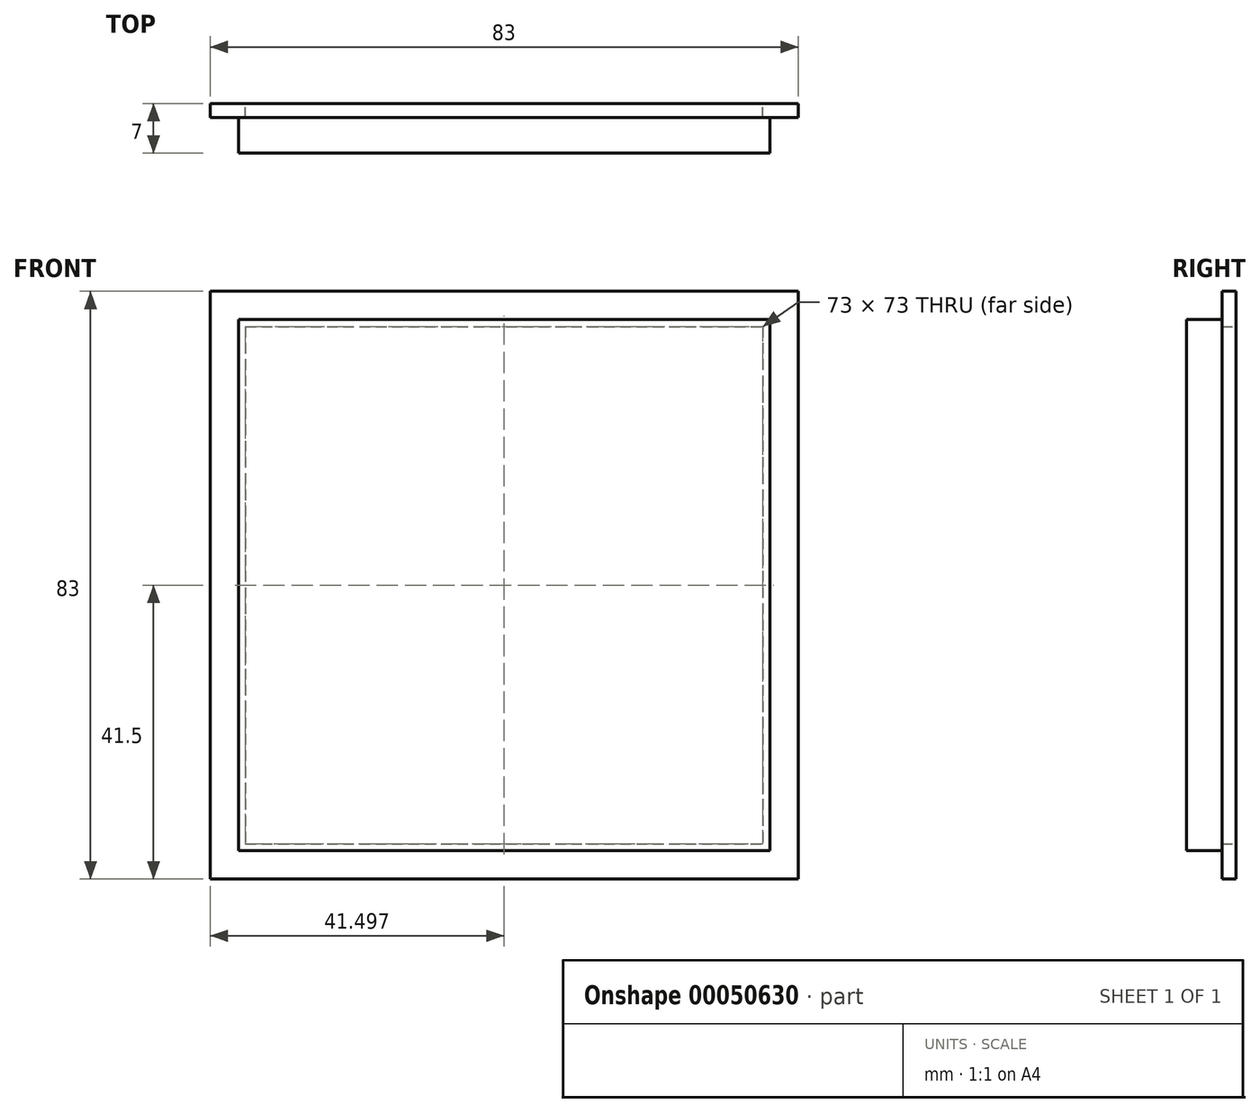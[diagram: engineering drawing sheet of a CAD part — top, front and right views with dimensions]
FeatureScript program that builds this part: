
annotation { "Feature Type Name" : "Feature", "Feature Type Description" : "" }
export const myFeature = defineFeature(function(context is Context, id is Id, definition is map)
    precondition{}
    {
        {
            var Q0;
            Q0=qCreatedBy(makeId("Front.planeOp"),FACE);
            var sketch = newSketch(context, id + "F0", { "sketchPlane" : qUnion([Q0])});
            skLineSegment(sketch, "E0", {"start": v(36.13, 0) * mm, "end": v(36.13, 36.5) * mm});
            skLineSegment(sketch, "E1", {"start": v(36.13, 36.5) * mm, "end": v(-0.37, 36.5) * mm});
            skCircle(sketch, "E2", {"center": v(19.63, 0) * mm, "radius": 1.7 * mm});
            skCircle(sketch, "E3", {"center": v(-0.37, 20) * mm, "radius": 1.7 * mm});
            skCircle(sketch, "E4", {"center": v(19.63, 20) * mm, "radius": 4 * mm, "construction": true});
            skCircle(sketch, "E5", {"center": v(11.93, 0) * mm, "radius": 3 * mm});
            skCircle(sketch, "E6.MirrorC", {"center": v(-20.37, 0) * mm, "radius": 1.7 * mm});
            skCircle(sketch, "E7.MirrorC", {"center": v(-20.37, 20) * mm, "radius": 4 * mm, "construction": true});
            skLineSegment(sketch, "E8.MirrorCS", {"start": v(-36.87, 36.5) * mm, "end": v(-0.37, 36.5) * mm});
            skLineSegment(sketch, "E9.MirrorCS", {"start": v(-36.87, 0) * mm, "end": v(-36.87, 36.5) * mm});
            skCircle(sketch, "E10.MirrorC", {"center": v(-0.37, -20) * mm, "radius": 1.7 * mm});
            skCircle(sketch, "E11.MirrorC", {"center": v(19.63, -20) * mm, "radius": 4 * mm, "construction": true});
            skLineSegment(sketch, "E12.MirrorCS", {"start": v(36.13, -36.5) * mm, "end": v(-0.37, -36.5) * mm});
            skLineSegment(sketch, "E13.MirrorCS", {"start": v(36.13, 0) * mm, "end": v(36.13, -36.5) * mm});
            skLineSegment(sketch, "E14.MirrorCS", {"start": v(-36.87, -36.5) * mm, "end": v(-0.37, -36.5) * mm});
            skLineSegment(sketch, "E15.MirrorCS", {"start": v(-36.87, 0) * mm, "end": v(-36.87, -36.5) * mm});
            skCircle(sketch, "E16.MirrorC", {"center": v(-20.37, -20) * mm, "radius": 4 * mm, "construction": true});
            skLineSegment(sketch, "E17.bottom", {"start": v(23.63, 16) * mm, "end": v(15.52, 16) * mm, "construction": true});
            skLineSegment(sketch, "E17.top", {"start": v(23.63, 24.04) * mm, "end": v(15.52, 24.04) * mm, "construction": true});
            skLineSegment(sketch, "E17.left", {"start": v(23.63, 16) * mm, "end": v(23.63, 24.04) * mm, "construction": true});
            skLineSegment(sketch, "E17.right", {"start": v(15.52, 16) * mm, "end": v(15.52, 24.04) * mm, "construction": true});
            skLineSegment(sketch, "E18.MirrorCS", {"start": v(-24.37, 16) * mm, "end": v(-16.26, 16) * mm, "construction": true});
            skLineSegment(sketch, "E19.MirrorCS", {"start": v(-16.26, 16) * mm, "end": v(-16.26, 24.04) * mm, "construction": true});
            skLineSegment(sketch, "E20.MirrorCS", {"start": v(-24.37, 16) * mm, "end": v(-24.37, 24.04) * mm, "construction": true});
            skLineSegment(sketch, "E21.MirrorCS", {"start": v(-24.37, 24.04) * mm, "end": v(-16.26, 24.04) * mm, "construction": true});
            skLineSegment(sketch, "E22.MirrorCS", {"start": v(23.63, -16) * mm, "end": v(15.52, -16) * mm, "construction": true});
            skLineSegment(sketch, "E23.MirrorCS", {"start": v(23.63, -16) * mm, "end": v(23.63, -24.04) * mm, "construction": true});
            skLineSegment(sketch, "E24.MirrorCS", {"start": v(23.63, -24.04) * mm, "end": v(15.52, -24.04) * mm, "construction": true});
            skLineSegment(sketch, "E25.MirrorCS", {"start": v(15.52, -16) * mm, "end": v(15.52, -24.04) * mm, "construction": true});
            skLineSegment(sketch, "E26.MirrorCS", {"start": v(-24.37, -16) * mm, "end": v(-16.26, -16) * mm, "construction": true});
            skLineSegment(sketch, "E27.MirrorCS", {"start": v(-24.37, -16) * mm, "end": v(-24.37, -24.04) * mm, "construction": true});
            skLineSegment(sketch, "E28.MirrorCS", {"start": v(-24.37, -24.04) * mm, "end": v(-16.26, -24.04) * mm, "construction": true});
            skLineSegment(sketch, "E29.MirrorCS", {"start": v(-16.26, -16) * mm, "end": v(-16.26, -24.04) * mm, "construction": true});
            skSolve(sketch);
        }
        {
            var Q0;
            Q0=qCreatedBy(makeId("Front.planeOp"),FACE);
            var sketch = newSketch(context, id + "F1", { "sketchPlane" : qUnion([Q0])});
            skLineSegment(sketch, "E30.bottom", {"start": v(-36.87, 36.5) * mm, "end": v(36.13, 36.5) * mm});
            skLineSegment(sketch, "E30.top", {"start": v(-36.87, -36.5) * mm, "end": v(36.13, -36.5) * mm});
            skLineSegment(sketch, "E30.left", {"start": v(-36.87, 36.5) * mm, "end": v(-36.87, -36.5) * mm});
            skLineSegment(sketch, "E30.right", {"start": v(36.13, 36.5) * mm, "end": v(36.13, -36.5) * mm});
            skLineSegment(sketch, "E31.rect.left", {"start": v(41.13, -41.5) * mm, "end": v(41.13, 41.5) * mm});
            skPoint(sketch, "E31.rect.middle", {"position": v(0, 0) * mm});
            skLineSegment(sketch, "E32", {"start": v(-41.87, -41.5) * mm, "end": v(41.13, -41.5) * mm});
            skLineSegment(sketch, "E33", {"start": v(-41.87, -41.5) * mm, "end": v(-41.87, 41.5) * mm});
            skLineSegment(sketch, "E34", {"start": v(-41.87, 41.5) * mm, "end": v(41.13, 41.5) * mm});
            skSolve(sketch);
        }
        {
            var Q0;
            Q0=makeQuery(id+"F1.imprint","IMPRINT",FACE,{"disambiguationData":[TD([[makeQuery(id+"F1.imprint","IMPRINT",EDGE,{"derivedFrom":sQuery(id+"F1.wireOp",EDGE,"E30.bottom")}),1.0]])]});
            extrude(context, id + "F2", {"entities" : qUnion([Q0]), "depth" : 2 * mm});
        }
        {
            var Q0;
            Q0=makeQuery(id+"F2.opExtrude","CAP_FACE",FACE,{"disambiguationData":[OSD([sQuery(id+"F1.wireOp",EDGE,"E30.bottom"),sQuery(id+"F1.wireOp",EDGE,"E30.top"),sQuery(id+"F1.wireOp",EDGE,"E30.left"),sQuery(id+"F1.wireOp",EDGE,"E30.right"),sQuery(id+"F1.wireOp",EDGE,"E31.rect.bottom"),sQuery(id+"F1.wireOp",EDGE,"E31.rect.top"),sQuery(id+"F1.wireOp",EDGE,"E31.rect.left"),sQuery(id+"F1.wireOp",EDGE,"E31.rect.right")])],"isStart":false});
            var sketch = newSketch(context, id + "F3", { "sketchPlane" : qUnion([Q0])});
            skLineSegment(sketch, "E35.bottom", {"start": v(-37.87, 37.5) * mm, "end": v(37.13, 37.5) * mm});
            skLineSegment(sketch, "E35.top", {"start": v(-37.87, -37.5) * mm, "end": v(37.13, -37.5) * mm});
            skLineSegment(sketch, "E35.left", {"start": v(-37.87, 37.5) * mm, "end": v(-37.87, -37.5) * mm});
            skLineSegment(sketch, "E35.right", {"start": v(37.13, 37.5) * mm, "end": v(37.13, -37.5) * mm});
            skSolve(sketch);
        }
        {
            var Q0;
            Q0=qSketchRegion(id+"F3",true);
            var Q1;
            Q1=makeQuery(id+"F3.imprint","IMPRINT",FACE,{"disambiguationData":[TD([[makeQuery(id+"F3.imprint","IMPRINT",EDGE,{"derivedFrom":sQuery(id+"F3.wireOp",EDGE,"7164ffd1-b8a4-4fcf-ab82-e8e68da7fcb8.bottom")}),-1.0]])]});
            extrude(context, id + "F4", {"entities" : qUnion([Q0, Q1]), "depth" : 5 * mm});
        }
    });
